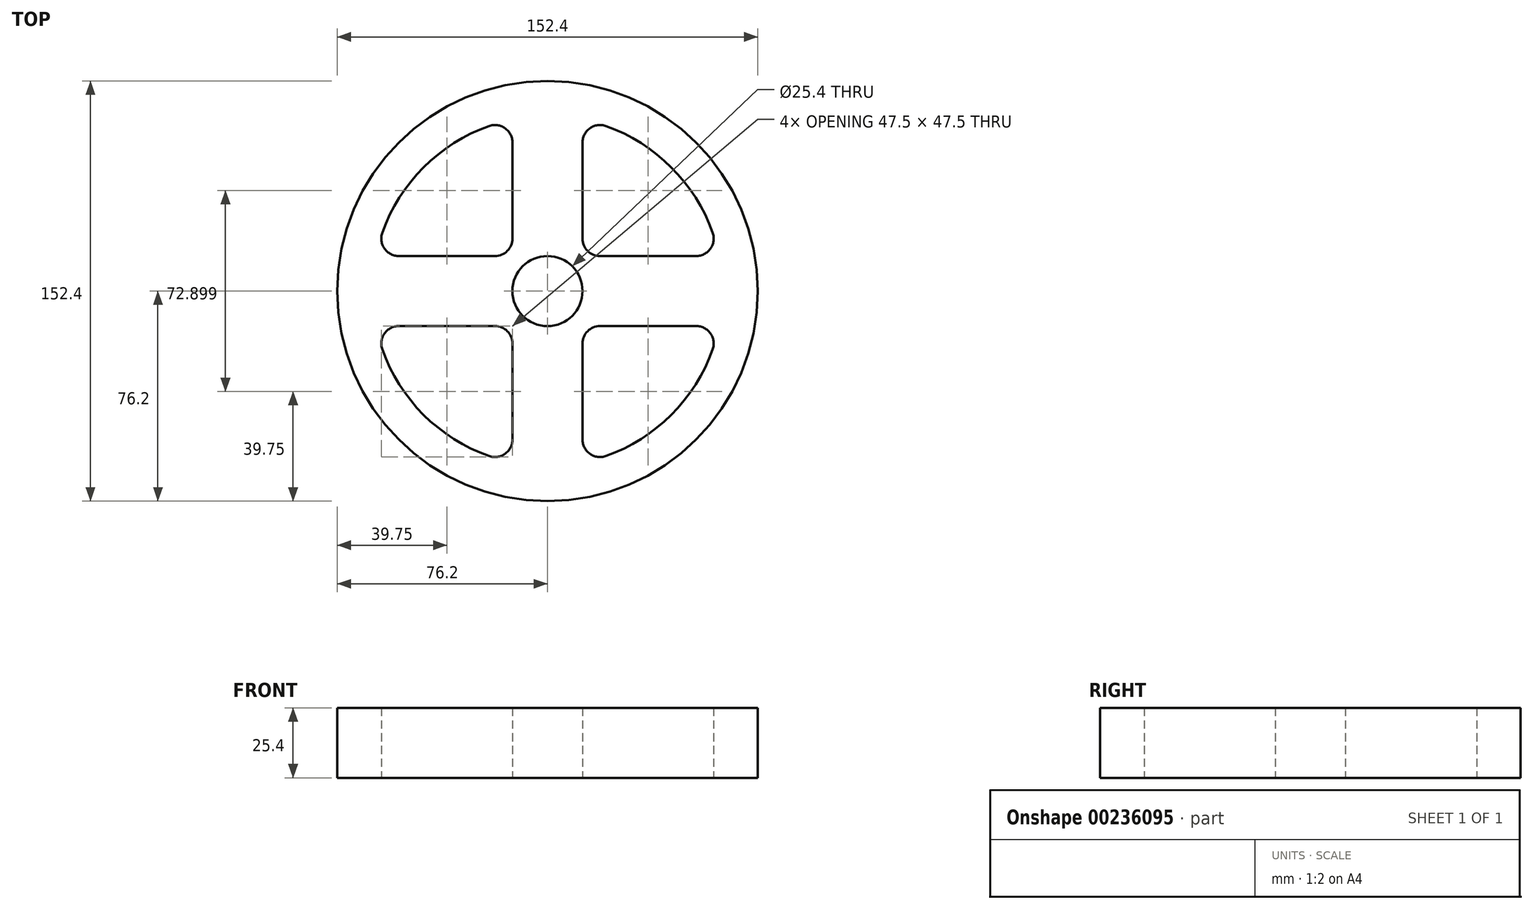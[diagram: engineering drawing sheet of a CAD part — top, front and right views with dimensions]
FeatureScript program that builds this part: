
annotation { "Feature Type Name" : "Feature", "Feature Type Description" : "" }
export const myFeature = defineFeature(function(context is Context, id is Id, definition is map)
    precondition{}
    {
        {
            var Q0;
            Q0=qCreatedBy(makeId("Top.planeOp"),FACE);
            var sketch = newSketch(context, id + "F0", { "sketchPlane" : qUnion([Q0])});
            skCircle(sketch, "E0", {"center": v(0, 0) * mm, "radius": 76.2 * mm});
            skArc(sketch, "E1", {"start": v(-59.87, -21.17) * mm, "mid": v(-44.9, -44.9) * mm, "end": v(-21.17, -59.87) * mm});
            skCircle(sketch, "E2", {"center": v(0, 0) * mm, "radius": 12.7 * mm});
            skLineSegment(sketch, "E3", {"start": v(0, 0) * mm, "end": v(0, 76.2) * mm});
            skLineSegment(sketch, "E4.0", {"start": v(12.7, 19.05) * mm, "end": v(12.7, 53.88) * mm});
            skLineSegment(sketch, "E5.0", {"start": v(-12.7, 19.05) * mm, "end": v(-12.7, 53.88) * mm});
            skLineSegment(sketch, "E6", {"start": v(0, 0) * mm, "end": v(-76.2, 0) * mm});
            skLineSegment(sketch, "E7", {"start": v(0, 0) * mm, "end": v(0, -76.2) * mm});
            skLineSegment(sketch, "E8", {"start": v(0, 0) * mm, "end": v(76.2, 0) * mm});
            skLineSegment(sketch, "E9.0", {"start": v(-19.05, 12.7) * mm, "end": v(-53.88, 12.7) * mm});
            skLineSegment(sketch, "E10.0", {"start": v(-12.7, -19.05) * mm, "end": v(-12.7, -53.88) * mm});
            skLineSegment(sketch, "E11.0", {"start": v(19.05, -12.7) * mm, "end": v(53.88, -12.7) * mm});
            skLineSegment(sketch, "E12.0", {"start": v(12.7, -19.05) * mm, "end": v(12.7, -53.88) * mm});
            skLineSegment(sketch, "E13.0", {"start": v(-19.05, -12.7) * mm, "end": v(-53.88, -12.7) * mm});
            skLineSegment(sketch, "E14.0", {"start": v(19.05, 12.7) * mm, "end": v(53.88, 12.7) * mm});
            skArc(sketch, "E15.trimOffspring", {"start": v(59.87, 21.17) * mm, "mid": v(44.9, 44.9) * mm, "end": v(21.17, 59.87) * mm});
            skArc(sketch, "E16.trimOffspring", {"start": v(21.17, -59.87) * mm, "mid": v(44.9, -44.9) * mm, "end": v(59.87, -21.17) * mm});
            skArc(sketch, "E17.trimOffspring", {"start": v(-21.17, 59.87) * mm, "mid": v(-44.9, 44.9) * mm, "end": v(-59.87, 21.17) * mm});
            skLineSegment(sketch, "E18.trimOffspring", {"start": v(-12.7, 75.13) * mm, "end": v(-12.7, 76.2) * mm});
            skLineSegment(sketch, "E19.trimOffspring", {"start": v(12.7, 75.13) * mm, "end": v(12.7, 76.2) * mm});
            skLineSegment(sketch, "E20.trimOffspring", {"start": v(75.13, 12.7) * mm, "end": v(76.2, 12.7) * mm});
            skLineSegment(sketch, "E21.trimOffspring", {"start": v(75.13, -12.7) * mm, "end": v(76.2, -12.7) * mm});
            skLineSegment(sketch, "E22.trimOffspring", {"start": v(-75.13, -12.7) * mm, "end": v(-76.2, -12.7) * mm});
            skLineSegment(sketch, "E23.trimOffspring", {"start": v(-75.13, 12.7) * mm, "end": v(-76.2, 12.7) * mm});
            skLineSegment(sketch, "E24.trimOffspring", {"start": v(-12.7, -75.13) * mm, "end": v(-12.7, -76.2) * mm});
            skLineSegment(sketch, "E25.trimOffspring", {"start": v(12.7, -75.13) * mm, "end": v(12.7, -76.2) * mm});
            skPoint(sketch, "E26.visualSharp", {"position": v(12.7, 12.7) * mm});
            skArc(sketch, "E26.filletArc", {"start": v(12.7, 19.05) * mm, "mid": v(14.56, 14.56) * mm, "end": v(19.05, 12.7) * mm});
            skPoint(sketch, "E27.visualSharp", {"position": v(62.22, 12.7) * mm});
            skArc(sketch, "E27.filletArc", {"start": v(53.88, 12.7) * mm, "mid": v(59.07, 15.38) * mm, "end": v(59.87, 21.17) * mm});
            skPoint(sketch, "E28.visualSharp", {"position": v(12.7, 62.22) * mm});
            skArc(sketch, "E28.filletArc", {"start": v(21.17, 59.87) * mm, "mid": v(15.38, 59.07) * mm, "end": v(12.7, 53.88) * mm});
            skPoint(sketch, "E29.visualSharp", {"position": v(62.22, -12.7) * mm});
            skArc(sketch, "E29.filletArc", {"start": v(59.87, -21.17) * mm, "mid": v(59.07, -15.38) * mm, "end": v(53.88, -12.7) * mm});
            skPoint(sketch, "E30.visualSharp", {"position": v(12.7, -12.7) * mm});
            skArc(sketch, "E30.filletArc", {"start": v(19.05, -12.7) * mm, "mid": v(14.56, -14.56) * mm, "end": v(12.7, -19.05) * mm});
            skPoint(sketch, "E31.visualSharp", {"position": v(12.7, -62.22) * mm});
            skArc(sketch, "E31.filletArc", {"start": v(12.7, -53.88) * mm, "mid": v(15.38, -59.07) * mm, "end": v(21.17, -59.87) * mm});
            skPoint(sketch, "E32.visualSharp", {"position": v(-12.7, -62.22) * mm});
            skArc(sketch, "E32.filletArc", {"start": v(-21.17, -59.87) * mm, "mid": v(-15.38, -59.07) * mm, "end": v(-12.7, -53.88) * mm});
            skPoint(sketch, "E33.visualSharp", {"position": v(-12.7, -12.7) * mm});
            skArc(sketch, "E33.filletArc", {"start": v(-12.7, -19.05) * mm, "mid": v(-14.56, -14.56) * mm, "end": v(-19.05, -12.7) * mm});
            skPoint(sketch, "E34.visualSharp", {"position": v(-62.22, -12.7) * mm});
            skArc(sketch, "E34.filletArc", {"start": v(-53.88, -12.7) * mm, "mid": v(-59.07, -15.38) * mm, "end": v(-59.87, -21.17) * mm});
            skPoint(sketch, "E35.visualSharp", {"position": v(-12.7, 12.7) * mm});
            skArc(sketch, "E35.filletArc", {"start": v(-19.05, 12.7) * mm, "mid": v(-14.56, 14.56) * mm, "end": v(-12.7, 19.05) * mm});
            skPoint(sketch, "E36.visualSharp", {"position": v(-62.22, 12.7) * mm});
            skArc(sketch, "E36.filletArc", {"start": v(-59.87, 21.17) * mm, "mid": v(-59.07, 15.38) * mm, "end": v(-53.88, 12.7) * mm});
            skPoint(sketch, "E37.visualSharp", {"position": v(-12.7, 62.22) * mm});
            skArc(sketch, "E37.filletArc", {"start": v(-12.7, 53.88) * mm, "mid": v(-15.38, 59.07) * mm, "end": v(-21.17, 59.87) * mm});
            skLineSegment(sketch, "E38", {"start": v(0, 0) * mm, "end": v(-12.7, 12.7) * mm});
            skLineSegment(sketch, "E39", {"start": v(0, 0) * mm, "end": v(12.7, 12.7) * mm});
            skLineSegment(sketch, "E40", {"start": v(0, 0) * mm, "end": v(12.7, -12.7) * mm});
            skLineSegment(sketch, "E41", {"start": v(0, 0) * mm, "end": v(-12.7, -12.7) * mm});
            skSolve(sketch);
        }
        {
            var Q0;
            Q0 = qSketchRegion(id + "F0", true);
            extrude(context, id + "F1", {"entities" : qUnion([Q0]), "endBound" : BoundingType.SYMMETRIC, "depth" : 25.4 * mm});
        }
    });
